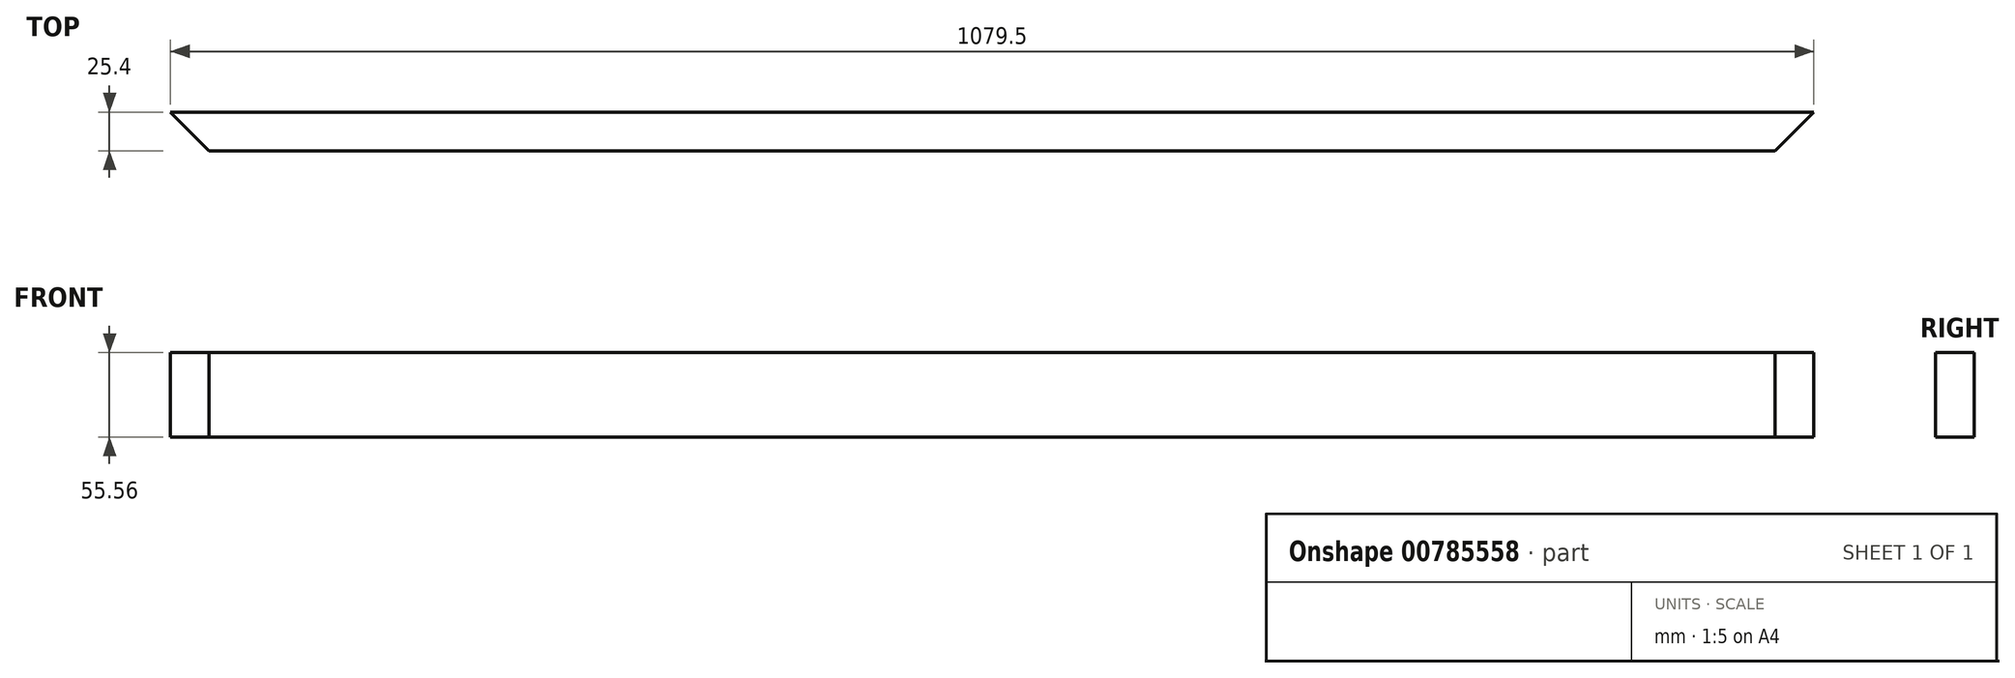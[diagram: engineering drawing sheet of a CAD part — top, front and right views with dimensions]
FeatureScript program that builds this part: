
annotation { "Feature Type Name" : "Feature", "Feature Type Description" : "" }
export const myFeature = defineFeature(function(context is Context, id is Id, definition is map)
    precondition{}
    {
        {
            var Q0;
            Q0=qCreatedBy(makeId("Top.planeOp"),FACE);
            var sketch = newSketch(context, id + "F0", { "sketchPlane" : qUnion([Q0])});
            skLineSegment(sketch, "E0.bottom", {"start": v(539.75, 12.7) * mm, "end": v(-539.75, 12.7) * mm});
            skLineSegment(sketch, "E0.top", {"start": v(539.75, -12.7) * mm, "end": v(-539.75, -12.7) * mm});
            skLineSegment(sketch, "E0.left", {"start": v(539.75, 12.7) * mm, "end": v(539.75, -12.7) * mm});
            skLineSegment(sketch, "E0.right", {"start": v(-539.75, 12.7) * mm, "end": v(-539.75, -12.7) * mm});
            skPoint(sketch, "E0.middle", {"position": v(0, 0) * mm});
            skLineSegment(sketch, "E1", {"start": v(-539.75, 12.7) * mm, "end": v(-514.35, -12.7) * mm});
            skLineSegment(sketch, "E2.MirrorCS", {"start": v(539.75, 12.7) * mm, "end": v(514.35, -12.7) * mm});
            skSolve(sketch);
        }
        {
            var Q0;
            Q0=makeQuery(id+"F0.imprint","IMPRINT",FACE,{"disambiguationData":[TD([[makeQuery(id+"F0.imprint","IMPRINT",EDGE,{"derivedFrom":sQuery(id+"F0.wireOp",EDGE,"E0.bottom")}),1.0]])]});
            extrude(context, id + "F1", {"entities" : qUnion([Q0]), "depth" : 55.56 * mm, "offsetDistance" : 25.4 * mm});
        }
    });
